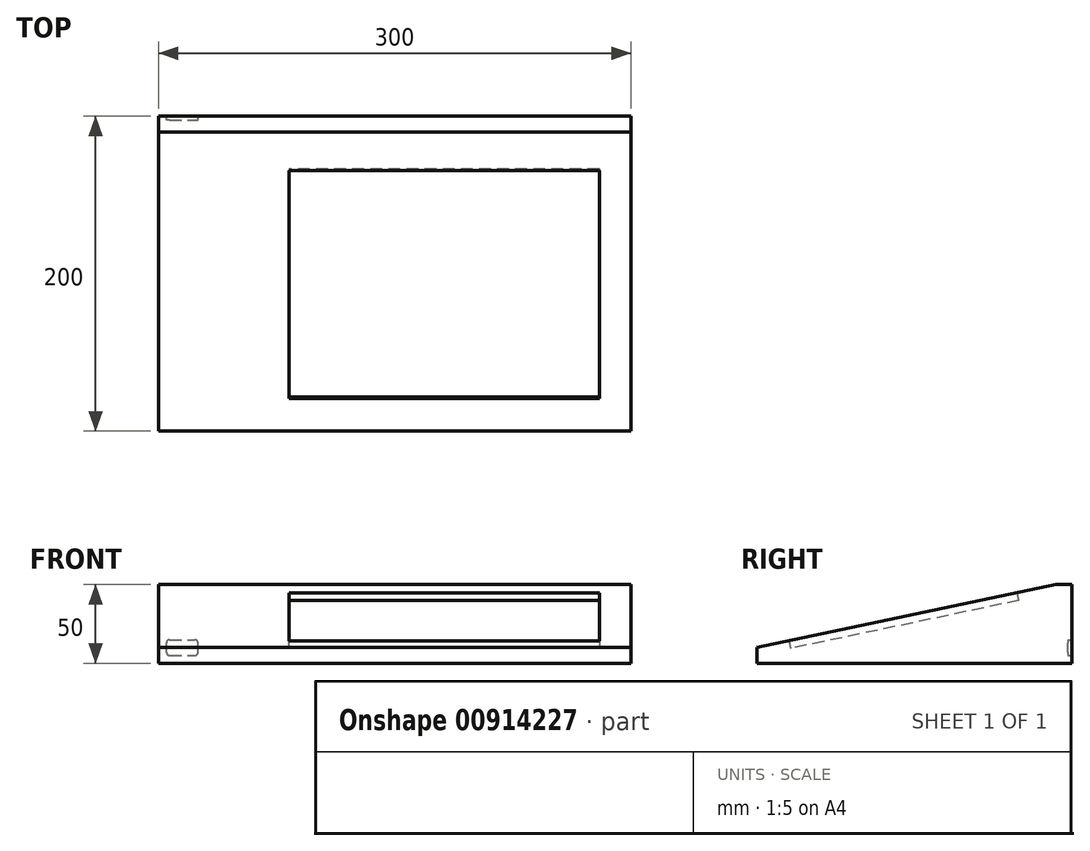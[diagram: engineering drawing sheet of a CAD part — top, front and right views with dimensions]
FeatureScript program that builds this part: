
annotation { "Feature Type Name" : "Feature", "Feature Type Description" : "" }
export const myFeature = defineFeature(function(context is Context, id is Id, definition is map)
    precondition{}
    {
        {
            var Q0;
            Q0=qCreatedBy(makeId("Right.planeOp"),FACE);
            var sketch = newSketch(context, id + "F0", { "sketchPlane" : qUnion([Q0])});
            skLineSegment(sketch, "E0", {"start": v(-200, 0) * mm, "end": v(0, 0) * mm});
            skLineSegment(sketch, "E1", {"start": v(0, 0) * mm, "end": v(0, 50) * mm});
            skLineSegment(sketch, "E2", {"start": v(-200, 10) * mm, "end": v(-200, 0) * mm});
            skLineSegment(sketch, "E3", {"start": v(0, 50) * mm, "end": v(-10, 50) * mm});
            skLineSegment(sketch, "E4", {"start": v(-10, 50) * mm, "end": v(-200, 10) * mm});
            skSolve(sketch);
        }
        {
            var Q0;
            Q0=makeQuery(id+"F0.imprint","IMPRINT",FACE,{"disambiguationData":[TD([[makeQuery(id+"F0.imprint","IMPRINT",EDGE,{"derivedFrom":sQuery(id+"F0.wireOp",EDGE,"E0")}),1.0]])]});
            extrude(context, id + "F1", {"entities" : qUnion([Q0]), "oppositeDirection" : true, "depth" : 300 * mm, "offsetDistance" : 25 * mm});
        }
        {
            var Q0;
            Q0=makeQuery(id+"F1.opExtrude","SWEPT_FACE",FACE,{"disambiguationData":[OSD([sQuery(id+"F0.wireOp",EDGE,"E4")])]});
            cPlane(context, id + "F2", {"entities" : qUnion([Q0]), "cplaneType" : CPlaneType.OFFSET, "offset" : 0 * mm, "width" : 150 * mm, "height" : 150 * mm});
        }
        {
            var Q0;
            Q0=qCreatedBy(id+"F2.planeOp",FACE);
            var sketch = newSketch(context, id + "F3", { "sketchPlane" : qUnion([Q0])});
            skLineSegment(sketch, "E5.bottom", {"start": v(-20, -24.48) * mm, "end": v(-217, -24.48) * mm});
            skLineSegment(sketch, "E5.top", {"start": v(-20, -172.48) * mm, "end": v(-217, -172.48) * mm});
            skLineSegment(sketch, "E5.left", {"start": v(-20, -24.48) * mm, "end": v(-20, -172.48) * mm});
            skLineSegment(sketch, "E5.right", {"start": v(-217, -24.48) * mm, "end": v(-217, -172.48) * mm});
            skSolve(sketch);
        }
        {
            var Q0;
            Q0=makeQuery(id+"F3.imprint","IMPRINT",FACE,{"disambiguationData":[TD([[makeQuery(id+"F3.imprint","IMPRINT",EDGE,{"derivedFrom":sQuery(id+"F3.wireOp",EDGE,"E5.bottom")}),1.0]])]});
            extrude(context, id + "F4", {"entities" : qUnion([Q0]), "operationType" : NewBodyOperationType.REMOVE, "oppositeDirection" : true, "depth" : 5 * mm, "offsetDistance" : 25 * mm});
        }
        {
            var Q0;
            Q0=makeQuery(id+"F1.opExtrude","SWEPT_FACE",FACE,{"disambiguationData":[OSD([sQuery(id+"F0.wireOp",EDGE,"E1")])]});
            var sketch = newSketch(context, id + "F5", { "sketchPlane" : qUnion([Q0])});
            skLineSegment(sketch, "E6.bottom", {"start": v(293, 5) * mm, "end": v(277, 5) * mm});
            skLineSegment(sketch, "E6.top", {"start": v(293, 15) * mm, "end": v(277, 15) * mm});
            skLineSegment(sketch, "E6.left", {"start": v(295, 7) * mm, "end": v(295, 13) * mm});
            skLineSegment(sketch, "E6.right", {"start": v(275, 7) * mm, "end": v(275, 13) * mm});
            skPoint(sketch, "E7.visualSharp", {"position": v(275, 15) * mm});
            skArc(sketch, "E7.filletArc", {"start": v(277, 15) * mm, "mid": v(275.59, 14.41) * mm, "end": v(275, 13) * mm});
            skPoint(sketch, "E8.visualSharp", {"position": v(295, 15) * mm});
            skArc(sketch, "E8.filletArc", {"start": v(295, 13) * mm, "mid": v(294.41, 14.41) * mm, "end": v(293, 15) * mm});
            skPoint(sketch, "E9.visualSharp", {"position": v(275, 5) * mm});
            skArc(sketch, "E9.filletArc", {"start": v(275, 7) * mm, "mid": v(275.59, 5.59) * mm, "end": v(277, 5) * mm});
            skPoint(sketch, "E10.visualSharp", {"position": v(295, 5) * mm});
            skArc(sketch, "E10.filletArc", {"start": v(293, 5) * mm, "mid": v(294.41, 5.59) * mm, "end": v(295, 7) * mm});
            skSolve(sketch);
        }
        {
            var Q0;
            Q0=makeQuery(id+"F5.imprint","IMPRINT",FACE,{"disambiguationData":[TD([[makeQuery(id+"F5.imprint","IMPRINT",EDGE,{"derivedFrom":sQuery(id+"F5.wireOp",EDGE,"E6.bottom")}),-1.0]])]});
            extrude(context, id + "F6", {"entities" : qUnion([Q0]), "operationType" : NewBodyOperationType.REMOVE, "oppositeDirection" : true, "depth" : 2.4 * mm, "offsetDistance" : 25 * mm});
        }
    });
